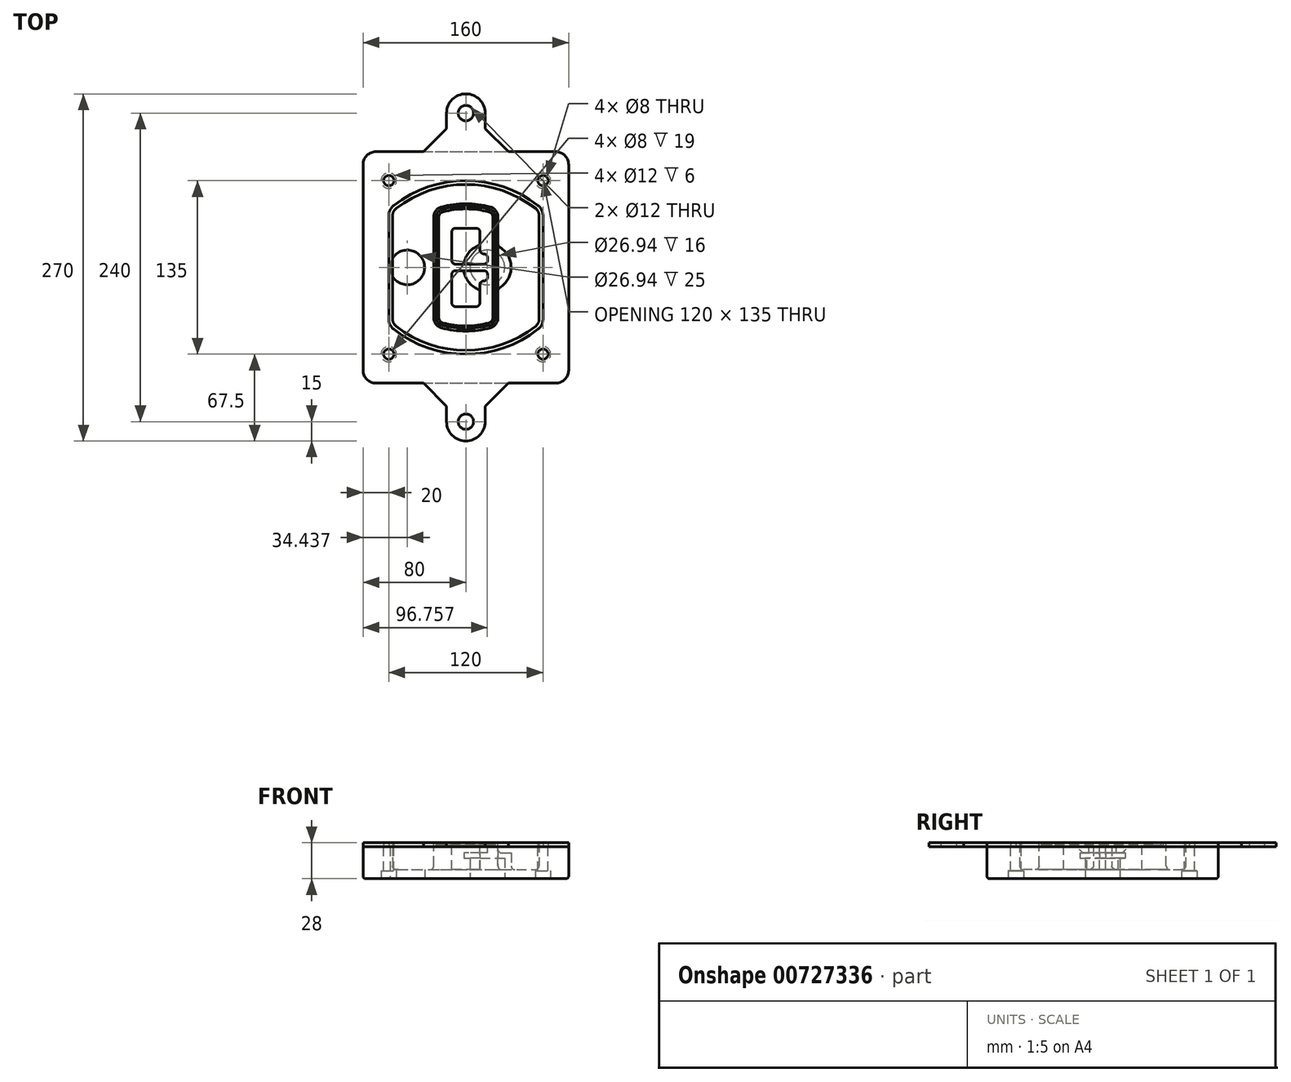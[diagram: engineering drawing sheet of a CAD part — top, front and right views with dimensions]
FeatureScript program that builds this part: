
annotation { "Feature Type Name" : "Feature", "Feature Type Description" : "" }
export const myFeature = defineFeature(function(context is Context, id is Id, definition is map)
    precondition{}
    {
        {
            var Q0;
            Q0=qCreatedBy(makeId("Top.planeOp"),FACE);
            var sketch = newSketch(context, id + "F0", { "sketchPlane" : qUnion([Q0])});
            skPoint(sketch, "E0.rect.middle", {"position": v(0, 0) * mm});
            skLineSegment(sketch, "E1.bottom", {"start": v(-70, -90) * mm, "end": v(70, -90) * mm});
            skLineSegment(sketch, "E1.top", {"start": v(-70, 90) * mm, "end": v(70, 90) * mm});
            skLineSegment(sketch, "E1.left", {"start": v(-80, -80) * mm, "end": v(-80, 80) * mm});
            skLineSegment(sketch, "E1.right", {"start": v(80, -80) * mm, "end": v(80, 80) * mm});
            skLineSegment(sketch, "E2", {"start": v(-80, 90) * mm, "end": v(80, -90) * mm, "construction": true});
            skLineSegment(sketch, "E3", {"start": v(80, 90) * mm, "end": v(-80, -90) * mm, "construction": true});
            skCircle(sketch, "E4", {"center": v(-60, 67.5) * mm, "radius": 4 * mm});
            skCircle(sketch, "E5", {"center": v(60, 67.5) * mm, "radius": 4 * mm});
            skCircle(sketch, "E6", {"center": v(60, -67.5) * mm, "radius": 4 * mm});
            skCircle(sketch, "E7", {"center": v(-60, -67.5) * mm, "radius": 4 * mm});
            skLineSegment(sketch, "E8", {"start": v(-60, 67.5) * mm, "end": v(60, 67.5) * mm, "construction": true});
            skLineSegment(sketch, "E9", {"start": v(60, 67.5) * mm, "end": v(60, -67.5) * mm, "construction": true});
            skLineSegment(sketch, "E10", {"start": v(60, -67.5) * mm, "end": v(-60, -67.5) * mm, "construction": true});
            skLineSegment(sketch, "E11", {"start": v(-60, -67.5) * mm, "end": v(-60, 67.5) * mm, "construction": true});
            skLineSegment(sketch, "E12", {"start": v(-60, 40.3) * mm, "end": v(-60, -40.3) * mm});
            skLineSegment(sketch, "E13", {"start": v(60, 40.3) * mm, "end": v(60, -40.3) * mm});
            skArc(sketch, "E14", {"start": v(56.15, 48.18) * mm, "mid": v(0, 67.5) * mm, "end": v(-56.15, 48.18) * mm});
            skArc(sketch, "E15", {"start": v(-56.15, -48.18) * mm, "mid": v(0, -67.5) * mm, "end": v(56.15, -48.18) * mm});
            skLineSegment(sketch, "E16", {"start": v(-60, 0) * mm, "end": v(60, 0) * mm, "construction": true});
            skPoint(sketch, "E17.visualSharp", {"position": v(-60, -45) * mm});
            skArc(sketch, "E17.filletArc", {"start": v(-60, -40.3) * mm, "mid": v(-58.99, -44.68) * mm, "end": v(-56.15, -48.18) * mm});
            skPoint(sketch, "E18.visualSharp", {"position": v(-60, 45) * mm});
            skArc(sketch, "E18.filletArc", {"start": v(-56.15, 48.18) * mm, "mid": v(-58.99, 44.68) * mm, "end": v(-60, 40.3) * mm});
            skPoint(sketch, "E19.visualSharp", {"position": v(60, 45) * mm});
            skArc(sketch, "E19.filletArc", {"start": v(60, 40.3) * mm, "mid": v(58.99, 44.68) * mm, "end": v(56.15, 48.18) * mm});
            skPoint(sketch, "E20.visualSharp", {"position": v(60, -45) * mm});
            skArc(sketch, "E20.filletArc", {"start": v(56.15, -48.18) * mm, "mid": v(58.99, -44.68) * mm, "end": v(60, -40.3) * mm});
            skPoint(sketch, "E21.visualSharp", {"position": v(-80, 90) * mm});
            skArc(sketch, "E21.filletArc", {"start": v(-70, 90) * mm, "mid": v(-77.07, 87.07) * mm, "end": v(-80, 80) * mm});
            skPoint(sketch, "E22.visualSharp", {"position": v(80, 90) * mm});
            skArc(sketch, "E22.filletArc", {"start": v(80, 80) * mm, "mid": v(77.07, 87.07) * mm, "end": v(70, 90) * mm});
            skPoint(sketch, "E23.visualSharp", {"position": v(80, -90) * mm});
            skArc(sketch, "E23.filletArc", {"start": v(70, -90) * mm, "mid": v(77.07, -87.07) * mm, "end": v(80, -80) * mm});
            skPoint(sketch, "E24.visualSharp", {"position": v(-80, -90) * mm});
            skArc(sketch, "E24.filletArc", {"start": v(-80, -80) * mm, "mid": v(-77.07, -87.07) * mm, "end": v(-70, -90) * mm});
            skArc(sketch, "E25.0", {"start": v(57, 40.3) * mm, "mid": v(56.3, 43.36) * mm, "end": v(54.3, 45.81) * mm});
            skLineSegment(sketch, "E25.1", {"start": v(57, 40.3) * mm, "end": v(57, -40.3) * mm});
            skArc(sketch, "E25.2", {"start": v(54.3, -45.81) * mm, "mid": v(56.3, -43.36) * mm, "end": v(57, -40.3) * mm});
            skArc(sketch, "E25.3", {"start": v(-54.3, -45.81) * mm, "mid": v(0, -64.5) * mm, "end": v(54.3, -45.81) * mm});
            skArc(sketch, "E25.4", {"start": v(-57, -40.3) * mm, "mid": v(-56.3, -43.36) * mm, "end": v(-54.3, -45.81) * mm});
            skArc(sketch, "E25.5", {"start": v(54.3, 45.81) * mm, "mid": v(0, 64.5) * mm, "end": v(-54.3, 45.81) * mm});
            skLineSegment(sketch, "E25.6", {"start": v(-57, 40.3) * mm, "end": v(-57, -40.3) * mm});
            skArc(sketch, "E25.7", {"start": v(-54.3, 45.81) * mm, "mid": v(-56.3, 43.36) * mm, "end": v(-57, 40.3) * mm});
            skArc(sketch, "E26.0", {"start": v(-58.62, 51.33) * mm, "mid": v(-62.58, 46.43) * mm, "end": v(-64, 40.3) * mm});
            skArc(sketch, "E26.1", {"start": v(58.62, 51.33) * mm, "mid": v(0, 71.5) * mm, "end": v(-58.62, 51.33) * mm});
            skArc(sketch, "E26.2", {"start": v(64, 40.3) * mm, "mid": v(62.58, 46.43) * mm, "end": v(58.62, 51.33) * mm});
            skLineSegment(sketch, "E26.3", {"start": v(64, 40.3) * mm, "end": v(64, -40.3) * mm});
            skArc(sketch, "E26.4", {"start": v(58.62, -51.33) * mm, "mid": v(62.58, -46.43) * mm, "end": v(64, -40.3) * mm});
            skLineSegment(sketch, "E26.5", {"start": v(-64, 40.3) * mm, "end": v(-64, -40.3) * mm});
            skArc(sketch, "E26.6", {"start": v(-58.62, -51.33) * mm, "mid": v(0, -71.5) * mm, "end": v(58.62, -51.33) * mm});
            skArc(sketch, "E26.7", {"start": v(-64, -40.3) * mm, "mid": v(-62.58, -46.43) * mm, "end": v(-58.62, -51.33) * mm});
            skSolve(sketch);
        }
        {
            var Q0;
            Q0=makeQuery(id+"F0.imprint","IMPRINT",FACE,{"disambiguationData":[TD([[makeQuery(id+"F0.imprint","IMPRINT",EDGE,{"derivedFrom":sQuery(id+"F0.wireOp",EDGE,"E1.bottom")}),1.0]])]});
            var Q1;
            Q1=makeQuery(id+"F0.imprint","IMPRINT",FACE,{"disambiguationData":[TD([[makeQuery(id+"F0.imprint","IMPRINT",EDGE,{"derivedFrom":sQuery(id+"F0.wireOp",EDGE,"E12")}),1.0]])]});
            var Q2;
            Q2=makeQuery(id+"F0.imprint","IMPRINT",FACE,{"disambiguationData":[TD([[makeQuery(id+"F0.imprint","IMPRINT",EDGE,{"derivedFrom":sQuery(id+"F0.wireOp",EDGE,"E25.0")}),1.0]])]});
            var Q3;
            Q3=makeQuery(id+"F0.imprint","IMPRINT",FACE,{"disambiguationData":[TD([[makeQuery(id+"F0.imprint","IMPRINT",EDGE,{"derivedFrom":sQuery(id+"F0.wireOp",EDGE,"E12")}),-1.0]])]});
            extrude(context, id + "F1", {"entities" : qUnion([Q0, Q1, Q2, Q3]), "oppositeDirection" : true, "depth" : 25 * mm});
        }
        {
            var Q0;
            Q0=makeQuery(id+"F0.imprint","IMPRINT",FACE,{"disambiguationData":[TD([[makeQuery(id+"F0.imprint","IMPRINT",EDGE,{"derivedFrom":sQuery(id+"F0.wireOp",EDGE,"E12")}),1.0]])]});
            extrude(context, id + "F2", {"entities" : qUnion([Q0]), "operationType" : NewBodyOperationType.ADD, "depth" : 3 * mm});
        }
        {
            var Q0;
            Q0=makeQuery(id+"F0.imprint","IMPRINT",FACE,{"disambiguationData":[TD([[makeQuery(id+"F0.imprint","IMPRINT",EDGE,{"derivedFrom":sQuery(id+"F0.wireOp",EDGE,"E25.0")}),1.0]])]});
            extrude(context, id + "F3", {"entities" : qUnion([Q0]), "operationType" : NewBodyOperationType.REMOVE, "oppositeDirection" : true, "depth" : 18 * mm});
        }
        {
            var Q0;
            Q0=makeQuery(id+"F2.opExtrude","CAP_FACE",FACE,{"disambiguationData":[OSD([sQuery(id+"F0.wireOp",EDGE,"E12"),sQuery(id+"F0.wireOp",EDGE,"E13"),sQuery(id+"F0.wireOp",EDGE,"E14"),sQuery(id+"F0.wireOp",EDGE,"E15"),sQuery(id+"F0.wireOp",EDGE,"E17.filletArc"),sQuery(id+"F0.wireOp",EDGE,"E18.filletArc"),sQuery(id+"F0.wireOp",EDGE,"E19.filletArc"),sQuery(id+"F0.wireOp",EDGE,"E20.filletArc"),sQuery(id+"F0.wireOp",EDGE,"E25.0"),sQuery(id+"F0.wireOp",EDGE,"E25.1"),sQuery(id+"F0.wireOp",EDGE,"E25.2"),sQuery(id+"F0.wireOp",EDGE,"E25.3"),sQuery(id+"F0.wireOp",EDGE,"E25.4"),sQuery(id+"F0.wireOp",EDGE,"E25.5"),sQuery(id+"F0.wireOp",EDGE,"E25.6"),sQuery(id+"F0.wireOp",EDGE,"E25.7")])],"isStart":false});
            var sketch = newSketch(context, id + "F4", { "sketchPlane" : qUnion([Q0])});
            skArc(sketch, "E27.0", {"start": v(-19.08, -46.97) * mm, "mid": v(0, -49.5) * mm, "end": v(19.08, -46.97) * mm});
            skArc(sketch, "E28.0", {"start": v(19.08, 46.97) * mm, "mid": v(0, 49.5) * mm, "end": v(-19.08, 46.97) * mm});
            skLineSegment(sketch, "E29", {"start": v(-25, 39.25) * mm, "end": v(-25, -39.25) * mm});
            skLineSegment(sketch, "E30", {"start": v(25, 39.25) * mm, "end": v(25, -39.25) * mm});
            skLineSegment(sketch, "E31", {"start": v(-25, 45.1) * mm, "end": v(25, 45.1) * mm, "construction": true});
            skLineSegment(sketch, "E32", {"start": v(-25, -45.1) * mm, "end": v(25, -45.1) * mm, "construction": true});
            skPoint(sketch, "E33.visualSharp", {"position": v(-25, 45.1) * mm});
            skArc(sketch, "E33.filletArc", {"start": v(-19.08, 46.97) * mm, "mid": v(-23.35, 44.11) * mm, "end": v(-25, 39.25) * mm});
            skPoint(sketch, "E34.visualSharp", {"position": v(25, 45.1) * mm});
            skArc(sketch, "E34.filletArc", {"start": v(25, 39.25) * mm, "mid": v(23.35, 44.11) * mm, "end": v(19.08, 46.97) * mm});
            skPoint(sketch, "E35.visualSharp", {"position": v(25, -45.1) * mm});
            skArc(sketch, "E35.filletArc", {"start": v(19.08, -46.97) * mm, "mid": v(23.35, -44.11) * mm, "end": v(25, -39.25) * mm});
            skPoint(sketch, "E36.visualSharp", {"position": v(-25, -45.1) * mm});
            skArc(sketch, "E36.filletArc", {"start": v(-25, -39.25) * mm, "mid": v(-23.35, -44.11) * mm, "end": v(-19.08, -46.97) * mm});
            skArc(sketch, "E37.0", {"start": v(54.3, 45.81) * mm, "mid": v(0, 64.5) * mm, "end": v(-54.3, 45.81) * mm});
            skArc(sketch, "E37.1", {"start": v(-54.3, 45.81) * mm, "mid": v(-56.3, 43.36) * mm, "end": v(-57, 40.3) * mm});
            skLineSegment(sketch, "E37.2", {"start": v(-57, 40.3) * mm, "end": v(-57, -40.3) * mm});
            skArc(sketch, "E37.3", {"start": v(-57, -40.3) * mm, "mid": v(-56.3, -43.36) * mm, "end": v(-54.3, -45.81) * mm});
            skArc(sketch, "E37.4", {"start": v(-54.3, -45.81) * mm, "mid": v(0, -64.5) * mm, "end": v(54.3, -45.81) * mm});
            skArc(sketch, "E37.5", {"start": v(54.3, -45.81) * mm, "mid": v(56.3, -43.36) * mm, "end": v(57, -40.3) * mm});
            skLineSegment(sketch, "E37.6", {"start": v(57, 40.3) * mm, "end": v(57, -40.3) * mm});
            skArc(sketch, "E37.7", {"start": v(57, 40.3) * mm, "mid": v(56.3, 43.36) * mm, "end": v(54.3, 45.81) * mm});
            skLineSegment(sketch, "E38.0", {"start": v(23, 39.25) * mm, "end": v(23, -39.25) * mm});
            skArc(sketch, "E38.1", {"start": v(18.56, -45.04) * mm, "mid": v(21.76, -42.9) * mm, "end": v(23, -39.25) * mm});
            skArc(sketch, "E38.2", {"start": v(-18.56, -45.04) * mm, "mid": v(0, -47.5) * mm, "end": v(18.56, -45.04) * mm});
            skArc(sketch, "E38.3", {"start": v(-23, -39.25) * mm, "mid": v(-21.76, -42.9) * mm, "end": v(-18.56, -45.04) * mm});
            skLineSegment(sketch, "E38.4", {"start": v(-23, 39.25) * mm, "end": v(-23, -39.25) * mm});
            skArc(sketch, "E38.5", {"start": v(23, 39.25) * mm, "mid": v(21.76, 42.9) * mm, "end": v(18.56, 45.04) * mm});
            skArc(sketch, "E38.6", {"start": v(-18.56, 45.04) * mm, "mid": v(-21.76, 42.9) * mm, "end": v(-23, 39.25) * mm});
            skArc(sketch, "E38.7", {"start": v(18.56, 45.04) * mm, "mid": v(0, 47.5) * mm, "end": v(-18.56, 45.04) * mm});
            skArc(sketch, "E39.0", {"start": v(21, 39.25) * mm, "mid": v(20.18, 41.68) * mm, "end": v(18.04, 43.1) * mm});
            skLineSegment(sketch, "E39.1", {"start": v(21, 39.25) * mm, "end": v(21, -39.25) * mm});
            skArc(sketch, "E39.2", {"start": v(18.04, -43.1) * mm, "mid": v(20.18, -41.68) * mm, "end": v(21, -39.25) * mm});
            skArc(sketch, "E39.3", {"start": v(-18.04, -43.1) * mm, "mid": v(0, -45.5) * mm, "end": v(18.04, -43.1) * mm});
            skArc(sketch, "E39.4", {"start": v(-21, -39.25) * mm, "mid": v(-20.18, -41.68) * mm, "end": v(-18.04, -43.1) * mm});
            skArc(sketch, "E39.5", {"start": v(18.04, 43.1) * mm, "mid": v(0, 45.5) * mm, "end": v(-18.04, 43.1) * mm});
            skLineSegment(sketch, "E39.6", {"start": v(-21, 39.25) * mm, "end": v(-21, -39.25) * mm});
            skArc(sketch, "E39.7", {"start": v(-18.04, 43.1) * mm, "mid": v(-20.18, 41.68) * mm, "end": v(-21, 39.25) * mm});
            skLineSegment(sketch, "E40", {"start": v(-25, 0) * mm, "end": v(25, 0) * mm, "construction": true});
            skLineSegment(sketch, "E41", {"start": v(-11, 5.5) * mm, "end": v(-11, 27.5) * mm});
            skLineSegment(sketch, "E42", {"start": v(-8, 30.5) * mm, "end": v(8, 30.5) * mm});
            skLineSegment(sketch, "E43", {"start": v(11, 27.5) * mm, "end": v(11, 13.5) * mm});
            skLineSegment(sketch, "E44", {"start": v(14, 10.5) * mm, "end": v(14, 10.5) * mm});
            skLineSegment(sketch, "E45", {"start": v(17, 7.5) * mm, "end": v(17, 5.5) * mm});
            skLineSegment(sketch, "E46", {"start": v(14, 2.5) * mm, "end": v(-8, 2.5) * mm});
            skPoint(sketch, "E47.visualSharp", {"position": v(-11, 30.5) * mm});
            skArc(sketch, "E47.filletArc", {"start": v(-8, 30.5) * mm, "mid": v(-10.12, 29.62) * mm, "end": v(-11, 27.5) * mm});
            skPoint(sketch, "E48.visualSharp", {"position": v(11, 30.5) * mm});
            skArc(sketch, "E48.filletArc", {"start": v(11, 27.5) * mm, "mid": v(10.12, 29.62) * mm, "end": v(8, 30.5) * mm});
            skPoint(sketch, "E49.visualSharp", {"position": v(11, 10.5) * mm});
            skArc(sketch, "E49.filletArc", {"start": v(11, 13.5) * mm, "mid": v(11.88, 11.38) * mm, "end": v(14, 10.5) * mm});
            skPoint(sketch, "E50.visualSharp", {"position": v(17, 10.5) * mm});
            skArc(sketch, "E50.filletArc", {"start": v(17, 7.5) * mm, "mid": v(16.12, 9.62) * mm, "end": v(14, 10.5) * mm});
            skPoint(sketch, "E51.visualSharp", {"position": v(17, 2.5) * mm});
            skArc(sketch, "E51.filletArc", {"start": v(14, 2.5) * mm, "mid": v(16.12, 3.38) * mm, "end": v(17, 5.5) * mm});
            skPoint(sketch, "E52.visualSharp", {"position": v(-11, 2.5) * mm});
            skArc(sketch, "E52.filletArc", {"start": v(-11, 5.5) * mm, "mid": v(-10.12, 3.38) * mm, "end": v(-8, 2.5) * mm});
            skLineSegment(sketch, "E53.0.MirrorCS", {"start": v(14, -2.5) * mm, "end": v(-8, -2.5) * mm});
            skArc(sketch, "E54.0.MirrorCS", {"start": v(-11, -5.5) * mm, "mid": v(-10.12, -3.38) * mm, "end": v(-8, -2.5) * mm});
            skLineSegment(sketch, "E55.0.MirrorCS", {"start": v(-11, -5.5) * mm, "end": v(-11, -27.5) * mm});
            skArc(sketch, "E56.0.MirrorCS", {"start": v(-8, -30.5) * mm, "mid": v(-10.12, -29.62) * mm, "end": v(-11, -27.5) * mm});
            skLineSegment(sketch, "E57.0.MirrorCS", {"start": v(-8, -30.5) * mm, "end": v(8, -30.5) * mm});
            skArc(sketch, "E58.0.MirrorCS", {"start": v(11, -27.5) * mm, "mid": v(10.12, -29.62) * mm, "end": v(8, -30.5) * mm});
            skLineSegment(sketch, "E59.0.MirrorCS", {"start": v(11, -27.5) * mm, "end": v(11, -13.5) * mm});
            skArc(sketch, "E60.0.MirrorCS", {"start": v(11, -13.5) * mm, "mid": v(11.88, -11.38) * mm, "end": v(14, -10.5) * mm});
            skArc(sketch, "E61.0.MirrorCS", {"start": v(17, -7.5) * mm, "mid": v(16.12, -9.62) * mm, "end": v(14, -10.5) * mm});
            skLineSegment(sketch, "E62.0.MirrorCS", {"start": v(17, -7.5) * mm, "end": v(17, -5.5) * mm});
            skArc(sketch, "E63.0.MirrorCS", {"start": v(14, -2.5) * mm, "mid": v(16.12, -3.38) * mm, "end": v(17, -5.5) * mm});
            skSolve(sketch);
        }
        {
            var Q0;
            Q0=makeQuery(id+"F4.imprint","IMPRINT",FACE,{"disambiguationData":[TD([[makeQuery(id+"F4.imprint","IMPRINT",EDGE,{"derivedFrom":sQuery(id+"F4.wireOp",EDGE,"E27.0")}),1.0]])]});
            var Q1;
            Q1=makeQuery(id+"F4.imprint","IMPRINT",FACE,{"disambiguationData":[TD([[makeQuery(id+"F4.imprint","IMPRINT",EDGE,{"derivedFrom":sQuery(id+"F4.wireOp",EDGE,"E38.0")}),-1.0]])]});
            var Q2;
            Q2=makeQuery(id+"F4.imprint","IMPRINT",FACE,{"disambiguationData":[TD([[makeQuery(id+"F4.imprint","IMPRINT",EDGE,{"derivedFrom":sQuery(id+"F4.wireOp",EDGE,"E39.0")}),1.0]])]});
            extrude(context, id + "F5", {"entities" : qUnion([Q0, Q1, Q2]), "operationType" : NewBodyOperationType.ADD, "endBound" : BoundingType.UP_TO_NEXT, "oppositeDirection" : true, "depth" : 25 * mm});
        }
        {
            var Q0;
            Q0=makeQuery(id+"F4.imprint","IMPRINT",FACE,{"disambiguationData":[TD([[makeQuery(id+"F4.imprint","IMPRINT",EDGE,{"derivedFrom":sQuery(id+"F4.wireOp",EDGE,"E38.0")}),-1.0]])]});
            extrude(context, id + "F6", {"entities" : qUnion([Q0]), "operationType" : NewBodyOperationType.REMOVE, "oppositeDirection" : true, "depth" : 2 * mm});
        }
        {
            var Q0;
            Q0=makeQuery(id+"F1.opExtrude","CAP_FACE",FACE,{"disambiguationData":[OSD([sQuery(id+"F0.wireOp",EDGE,"E1.bottom"),sQuery(id+"F0.wireOp",EDGE,"E1.top"),sQuery(id+"F0.wireOp",EDGE,"E1.left"),sQuery(id+"F0.wireOp",EDGE,"E1.right"),sQuery(id+"F0.wireOp",EDGE,"E4"),sQuery(id+"F0.wireOp",EDGE,"E5"),sQuery(id+"F0.wireOp",EDGE,"E6"),sQuery(id+"F0.wireOp",EDGE,"E7"),sQuery(id+"F0.wireOp",EDGE,"E21.filletArc"),sQuery(id+"F0.wireOp",EDGE,"E22.filletArc"),sQuery(id+"F0.wireOp",EDGE,"E23.filletArc"),sQuery(id+"F0.wireOp",EDGE,"E24.filletArc")])],"isStart":false});
            var sketch = newSketch(context, id + "F7", { "sketchPlane" : qUnion([Q0])});
            skCircle(sketch, "E64", {"center": v(16.76, 0) * mm, "radius": 13.47 * mm});
            skCircle(sketch, "E65", {"center": v(-45.56, 0) * mm, "radius": 13.47 * mm});
            skLineSegment(sketch, "E66", {"start": v(80, 0) * mm, "end": v(-80, 0) * mm});
            skCircle(sketch, "E67", {"center": v(16.76, 0) * mm, "radius": 18.47 * mm});
            skCircle(sketch, "E68", {"center": v(60, -67.5) * mm, "radius": 6 * mm});
            skCircle(sketch, "E69", {"center": v(-60, -67.5) * mm, "radius": 6 * mm});
            skCircle(sketch, "E70", {"center": v(-60, 67.5) * mm, "radius": 6 * mm});
            skCircle(sketch, "E71", {"center": v(60, 67.5) * mm, "radius": 6 * mm});
            skSolve(sketch);
        }
        {
            var Q0;
            {var subQ1=sQuery(id+"F7.wireOp",EDGE,"E66");var subQ4=sQuery(id+"F7.wireOp",EDGE,"E64");var subQ6=makeQuery(id+"F7.imprint","INTERSECT",VERTEX,{"disambiguationData":[OD(0.0)],"derivedFrom":[subQ4,subQ1]});Q0=makeQuery(id+"F7.imprint","IMPRINT",FACE,{"disambiguationData":[TD([[makeQuery(id+"F7.imprint","IMPRINT",EDGE,{"disambiguationData":[TD([[subQ6,-1.0]])],"derivedFrom":subQ4}),-1.0]])]});}
            var Q1;
            {var subQ0=sQuery(id+"F7.wireOp",EDGE,"E66");var subQ1=sQuery(id+"F7.wireOp",EDGE,"E64");var subQ3=makeQuery(id+"F7.imprint","INTERSECT",VERTEX,{"disambiguationData":[OD(0.0)],"derivedFrom":[subQ1,subQ0]});Q1=makeQuery(id+"F7.imprint","IMPRINT",FACE,{"disambiguationData":[TD([[makeQuery(id+"F7.imprint","IMPRINT",EDGE,{"disambiguationData":[TD([[subQ3,-1.0]])],"derivedFrom":subQ1}),1.0]])]});}
            var Q2;
            {var subQ0=sQuery(id+"F7.wireOp",EDGE,"E66");var subQ1=sQuery(id+"F7.wireOp",EDGE,"E64");var subQ3=makeQuery(id+"F7.imprint","INTERSECT",VERTEX,{"disambiguationData":[OD(0.0)],"derivedFrom":[subQ1,subQ0]});Q2=makeQuery(id+"F7.imprint","IMPRINT",FACE,{"disambiguationData":[TD([[makeQuery(id+"F7.imprint","IMPRINT",EDGE,{"disambiguationData":[TD([[subQ3,1.0]])],"derivedFrom":subQ1}),1.0]])]});}
            var Q3;
            {var subQ1=sQuery(id+"F7.wireOp",EDGE,"E66");var subQ4=sQuery(id+"F7.wireOp",EDGE,"E64");var subQ6=makeQuery(id+"F7.imprint","INTERSECT",VERTEX,{"disambiguationData":[OD(0.0)],"derivedFrom":[subQ4,subQ1]});Q3=makeQuery(id+"F7.imprint","IMPRINT",FACE,{"disambiguationData":[TD([[makeQuery(id+"F7.imprint","IMPRINT",EDGE,{"disambiguationData":[TD([[subQ6,1.0]])],"derivedFrom":subQ4}),-1.0]])]});}
            extrude(context, id + "F8", {"entities" : qUnion([Q0, Q1, Q2, Q3]), "operationType" : NewBodyOperationType.ADD, "oppositeDirection" : true, "depth" : 20 * mm});
        }
        {
            var Q0;
            {var subQ0=sQuery(id+"F7.wireOp",EDGE,"E66");var subQ1=sQuery(id+"F7.wireOp",EDGE,"E64");var subQ3=makeQuery(id+"F7.imprint","INTERSECT",VERTEX,{"disambiguationData":[OD(0.0)],"derivedFrom":[subQ1,subQ0]});Q0=makeQuery(id+"F7.imprint","IMPRINT",FACE,{"disambiguationData":[TD([[makeQuery(id+"F7.imprint","IMPRINT",EDGE,{"disambiguationData":[TD([[subQ3,-1.0]])],"derivedFrom":subQ1}),1.0]])]});}
            var Q1;
            {var subQ0=sQuery(id+"F7.wireOp",EDGE,"E66");var subQ1=sQuery(id+"F7.wireOp",EDGE,"E64");var subQ3=makeQuery(id+"F7.imprint","INTERSECT",VERTEX,{"disambiguationData":[OD(0.0)],"derivedFrom":[subQ1,subQ0]});Q1=makeQuery(id+"F7.imprint","IMPRINT",FACE,{"disambiguationData":[TD([[makeQuery(id+"F7.imprint","IMPRINT",EDGE,{"disambiguationData":[TD([[subQ3,1.0]])],"derivedFrom":subQ1}),1.0]])]});}
            extrude(context, id + "F9", {"entities" : qUnion([Q0, Q1]), "operationType" : NewBodyOperationType.REMOVE, "oppositeDirection" : true, "depth" : 16 * mm});
        }
        {
            var Q0;
            {var subQ0=sQuery(id+"F7.wireOp",EDGE,"E66");var subQ1=sQuery(id+"F7.wireOp",EDGE,"E65");var subQ3=makeQuery(id+"F7.imprint","INTERSECT",VERTEX,{"disambiguationData":[OD(0.0)],"derivedFrom":[subQ1,subQ0]});Q0=makeQuery(id+"F7.imprint","IMPRINT",FACE,{"disambiguationData":[TD([[makeQuery(id+"F7.imprint","IMPRINT",EDGE,{"disambiguationData":[TD([[subQ3,-1.0]])],"derivedFrom":subQ1}),1.0]])]});}
            var Q1;
            {var subQ0=sQuery(id+"F7.wireOp",EDGE,"E66");var subQ1=sQuery(id+"F7.wireOp",EDGE,"E65");var subQ3=makeQuery(id+"F7.imprint","INTERSECT",VERTEX,{"disambiguationData":[OD(0.0)],"derivedFrom":[subQ1,subQ0]});Q1=makeQuery(id+"F7.imprint","IMPRINT",FACE,{"disambiguationData":[TD([[makeQuery(id+"F7.imprint","IMPRINT",EDGE,{"disambiguationData":[TD([[subQ3,1.0]])],"derivedFrom":subQ1}),1.0]])]});}
            extrude(context, id + "F10", {"entities" : qUnion([Q0, Q1]), "operationType" : NewBodyOperationType.REMOVE, "oppositeDirection" : true, "depth" : 25 * mm});
        }
        {
            var Q0;
            Q0=makeQuery(id+"F7.imprint","IMPRINT",FACE,{"disambiguationData":[TD([[makeQuery(id+"F7.imprint","IMPRINT",EDGE,{"derivedFrom":sQuery(id+"F7.wireOp",EDGE,"E68")}),1.0]])]});
            var Q1;
            Q1=makeQuery(id+"F7.imprint","IMPRINT",FACE,{"disambiguationData":[TD([[makeQuery(id+"F7.imprint","IMPRINT",EDGE,{"derivedFrom":makeQuery(id+"F1.opExtrude","CAP_EDGE",EDGE,{"disambiguationData":[OSD([sQuery(id+"F0.wireOp",EDGE,"E5")])],"isStart":false})}),-1.0]])]});
            var Q2;
            Q2=makeQuery(id+"F7.imprint","IMPRINT",FACE,{"disambiguationData":[TD([[makeQuery(id+"F7.imprint","IMPRINT",EDGE,{"derivedFrom":sQuery(id+"F7.wireOp",EDGE,"E69")}),1.0]])]});
            var Q3;
            Q3=makeQuery(id+"F7.imprint","IMPRINT",FACE,{"disambiguationData":[TD([[makeQuery(id+"F7.imprint","IMPRINT",EDGE,{"derivedFrom":makeQuery(id+"F1.opExtrude","CAP_EDGE",EDGE,{"disambiguationData":[OSD([sQuery(id+"F0.wireOp",EDGE,"E4")])],"isStart":false})}),-1.0]])]});
            var Q4;
            Q4=makeQuery(id+"F7.imprint","IMPRINT",FACE,{"disambiguationData":[TD([[makeQuery(id+"F7.imprint","IMPRINT",EDGE,{"derivedFrom":sQuery(id+"F7.wireOp",EDGE,"E70")}),1.0]])]});
            var Q5;
            Q5=makeQuery(id+"F7.imprint","IMPRINT",FACE,{"disambiguationData":[TD([[makeQuery(id+"F7.imprint","IMPRINT",EDGE,{"derivedFrom":makeQuery(id+"F1.opExtrude","CAP_EDGE",EDGE,{"disambiguationData":[OSD([sQuery(id+"F0.wireOp",EDGE,"E7")])],"isStart":false})}),-1.0]])]});
            var Q6;
            Q6=makeQuery(id+"F7.imprint","IMPRINT",FACE,{"disambiguationData":[TD([[makeQuery(id+"F7.imprint","IMPRINT",EDGE,{"derivedFrom":sQuery(id+"F7.wireOp",EDGE,"E71")}),1.0]])]});
            var Q7;
            Q7=makeQuery(id+"F7.imprint","IMPRINT",FACE,{"disambiguationData":[TD([[makeQuery(id+"F7.imprint","IMPRINT",EDGE,{"derivedFrom":makeQuery(id+"F1.opExtrude","CAP_EDGE",EDGE,{"disambiguationData":[OSD([sQuery(id+"F0.wireOp",EDGE,"E6")])],"isStart":false})}),-1.0]])]});
            extrude(context, id + "F11", {"entities" : qUnion([Q0, Q1, Q2, Q3, Q4, Q5, Q6, Q7]), "operationType" : NewBodyOperationType.REMOVE, "oppositeDirection" : true, "depth" : 6 * mm});
        }
        {
            var Q0;
            Q0=makeQuery(id+"F9.boolean.opBoolean","COPY",FACE,{"derivedFrom":makeQuery(id+"F9.opExtrude","CAP_FACE",FACE,{"disambiguationData":[OSD([sQuery(id+"F7.wireOp",EDGE,"E64")])],"isStart":false})});
            var sketch = newSketch(context, id + "F12", { "sketchPlane" : qUnion([Q0])});
            skArc(sketch, "E72.0", {"start": v(11, 17.55) * mm, "mid": v(2.57, 11.82) * mm, "end": v(-1.54, 2.5) * mm});
            skArc(sketch, "E72.1", {"start": v(-1.54, -2.5) * mm, "mid": v(2.57, -11.82) * mm, "end": v(11, -17.55) * mm});
            skLineSegment(sketch, "E73", {"start": v(-1.54, -2.5) * mm, "end": v(14, -2.5) * mm});
            skLineSegment(sketch, "E74.0", {"start": v(14, 2.5) * mm, "end": v(-1.54, 2.5) * mm});
            skArc(sketch, "E74.1", {"start": v(14, 2.5) * mm, "mid": v(16.12, 3.38) * mm, "end": v(17, 5.5) * mm});
            skLineSegment(sketch, "E74.2", {"start": v(17, 7.5) * mm, "end": v(17, 5.5) * mm});
            skArc(sketch, "E74.3", {"start": v(17, 7.5) * mm, "mid": v(16.12, 9.62) * mm, "end": v(14, 10.5) * mm});
            skArc(sketch, "E74.4", {"start": v(11, 13.5) * mm, "mid": v(11.88, 11.38) * mm, "end": v(14, 10.5) * mm});
            skLineSegment(sketch, "E74.5", {"start": v(11, 17.55) * mm, "end": v(11, 13.5) * mm});
            skLineSegment(sketch, "E74.7", {"start": v(14, -2.5) * mm, "end": v(-1.54, -2.5) * mm});
            skArc(sketch, "E74.8", {"start": v(14, -2.5) * mm, "mid": v(16.12, -3.38) * mm, "end": v(17, -5.5) * mm});
            skLineSegment(sketch, "E74.9", {"start": v(17, -7.5) * mm, "end": v(17, -5.5) * mm});
            skArc(sketch, "E74.10", {"start": v(17, -7.5) * mm, "mid": v(16.12, -9.62) * mm, "end": v(14, -10.5) * mm});
            skArc(sketch, "E74.11", {"start": v(11, -13.5) * mm, "mid": v(11.88, -11.38) * mm, "end": v(14, -10.5) * mm});
            skLineSegment(sketch, "E74.12", {"start": v(11, -17.55) * mm, "end": v(11, -13.5) * mm});
            skPoint(sketch, "E75.orphan", {"position": v(11, -27.5) * mm});
            skPoint(sketch, "E76.orphan", {"position": v(-8, -2.5) * mm});
            skPoint(sketch, "E77.orphan", {"position": v(-8, 2.5) * mm});
            skPoint(sketch, "E78.orphan", {"position": v(11, 27.5) * mm});
            skSolve(sketch);
        }
        {
            var Q0;
            {var subQ7=sQuery(id+"F12.wireOp",EDGE,"E72.0");var subQ14=sQuery(id+"F12.wireOp",EDGE,"E72.1");var subQ16=sQuery(id+"F12.wireOp",EDGE,"E74.1");var subQ18=sQuery(id+"F12.wireOp",EDGE,"E74.8");Q0=qUnion([makeQuery(id+"F12.imprint","IMPRINT",FACE,{"disambiguationData":[TD([[makeQuery(id+"F12.imprint","IMPRINT",EDGE,{"derivedFrom":subQ7}),1.0]])]}),makeQuery(id+"F12.imprint","IMPRINT",FACE,{"disambiguationData":[TD([[makeQuery(id+"F12.imprint","IMPRINT",EDGE,{"derivedFrom":subQ14}),1.0]])]}),makeQuery(id+"F12.imprint","IMPRINT",FACE,{"disambiguationData":[TD([[makeQuery(id+"F12.imprint","IMPRINT",EDGE,{"derivedFrom":subQ16}),1.0]])]}),makeQuery(id+"F12.imprint","IMPRINT",FACE,{"disambiguationData":[TD([[makeQuery(id+"F12.imprint","IMPRINT",EDGE,{"derivedFrom":subQ18}),-1.0]])]})]);}
            var Q1;
            Q1=makeQuery(id+"F5.boolean.opBoolean","SPLIT",FACE,{"disambiguationData":[TD([makeQuery(id+"F5.opExtrude","SWEPT_FACE",FACE,{"disambiguationData":[OSD([sQuery(id+"F4.wireOp",EDGE,"E41")])]})])],"derivedFrom":makeQuery(id+"F3.boolean.opBoolean","COPY",FACE,{"derivedFrom":makeQuery(id+"F3.opExtrude","CAP_FACE",FACE,{"disambiguationData":[OSD([sQuery(id+"F0.wireOp",EDGE,"E25.0"),sQuery(id+"F0.wireOp",EDGE,"E25.1"),sQuery(id+"F0.wireOp",EDGE,"E25.2"),sQuery(id+"F0.wireOp",EDGE,"E25.3"),sQuery(id+"F0.wireOp",EDGE,"E25.4"),sQuery(id+"F0.wireOp",EDGE,"E25.5"),sQuery(id+"F0.wireOp",EDGE,"E25.6"),sQuery(id+"F0.wireOp",EDGE,"E25.7")])],"isStart":false})})});
            extrude(context, id + "F13", {"entities" : qUnion([Q0]), "operationType" : NewBodyOperationType.REMOVE, "endBound" : BoundingType.UP_TO_SURFACE, "endBoundEntityFace" : qUnion([Q1]), "depth" : 25 * mm});
        }
        {
            var Q0;
            Q0=makeQuery(id+"F3.boolean.opBoolean","COPY",EDGE,{"derivedFrom":makeQuery(id+"F3.opExtrude","CAP_EDGE",EDGE,{"disambiguationData":[OSD([sQuery(id+"F0.wireOp",EDGE,"E25.6")])],"isStart":false})});
            var Q1;
            Q1=makeQuery(id+"F8.boolean.opBoolean","INTERSECT",EDGE,{"derivedFrom":[makeQuery(id+"F5.opExtrude","SWEPT_FACE",FACE,{"disambiguationData":[OSD([sQuery(id+"F4.wireOp",EDGE,"E30")])]}),makeQuery(id+"F8.opExtrude","CAP_FACE",FACE,{"disambiguationData":[OSD([sQuery(id+"F7.wireOp",EDGE,"E67")])],"isStart":false})]});
            var Q2;
            Q2=makeQuery(id+"F8.boolean.opBoolean","INTERSECT",EDGE,{"disambiguationData":[OD(1.0)],"derivedFrom":[makeQuery(id+"F5.opExtrude","SWEPT_FACE",FACE,{"disambiguationData":[OSD([sQuery(id+"F4.wireOp",EDGE,"E30")])]}),makeQuery(id+"F8.opExtrude","SWEPT_FACE",FACE,{"disambiguationData":[OSD([sQuery(id+"F7.wireOp",EDGE,"E67")])]})]});
            var Q3;
            {var subQ0=sQuery(id+"F4.wireOp",EDGE,"E30");Q3=makeQuery(id+"F8.boolean.opBoolean","SPLIT",EDGE,{"disambiguationData":[TD([makeQuery(id+"F5.opExtrude","SWEPT_FACE",FACE,{"disambiguationData":[OSD([sQuery(id+"F4.wireOp",EDGE,"E35.filletArc")])]})])],"derivedFrom":makeQuery(id+"F5.opExtrude","CAP_EDGE",EDGE,{"disambiguationData":[OSD([subQ0])],"isStart":false})});}
            var Q4;
            {var subQ0=sQuery(id+"F0.wireOp",EDGE,"E25.7");var subQ1=sQuery(id+"F0.wireOp",EDGE,"E25.1");var subQ2=sQuery(id+"F0.wireOp",EDGE,"E25.6");var subQ3=sQuery(id+"F0.wireOp",EDGE,"E25.5");var subQ4=sQuery(id+"F0.wireOp",EDGE,"E25.4");var subQ5=sQuery(id+"F0.wireOp",EDGE,"E25.0");var subQ6=sQuery(id+"F0.wireOp",EDGE,"E25.2");var subQ7=sQuery(id+"F0.wireOp",EDGE,"E25.3");Q4=makeQuery(id+"F8.boolean.opBoolean","INTERSECT",EDGE,{"derivedFrom":[makeQuery(id+"F5.boolean.opBoolean","SPLIT",FACE,{"disambiguationData":[TD([makeQuery(id+"F2.opExtrude","SWEPT_FACE",FACE,{"disambiguationData":[OSD([subQ5])]})])],"derivedFrom":makeQuery(id+"F3.boolean.opBoolean","COPY",FACE,{"derivedFrom":makeQuery(id+"F3.opExtrude","CAP_FACE",FACE,{"disambiguationData":[OSD([subQ5,subQ1,subQ6,subQ7,subQ4,subQ3,subQ2,subQ0])],"isStart":false})})}),makeQuery(id+"F8.opExtrude","SWEPT_FACE",FACE,{"disambiguationData":[OSD([sQuery(id+"F7.wireOp",EDGE,"E67")])]})]});}
            var Q5;
            Q5=makeQuery(id+"F8.boolean.opBoolean","INTERSECT",EDGE,{"disambiguationData":[OD(0.0)],"derivedFrom":[makeQuery(id+"F5.opExtrude","SWEPT_FACE",FACE,{"disambiguationData":[OSD([sQuery(id+"F4.wireOp",EDGE,"E30")])]}),makeQuery(id+"F8.opExtrude","SWEPT_FACE",FACE,{"disambiguationData":[OSD([sQuery(id+"F7.wireOp",EDGE,"E67")])]})]});
            fillet(context, id + "F14", {"entities" : qUnion([Q0, Q1, Q2, Q3, Q4, Q5]), "radius" : 3 * mm, "tangentPropagation" : true, "allowEdgeOverflow" : false});
        }
        {
            var Q0;
            Q0=makeQuery(id+"F1.opExtrude","CAP_EDGE",EDGE,{"disambiguationData":[OSD([sQuery(id+"F0.wireOp",EDGE,"E1.bottom")])],"isStart":false});
            fillet(context, id + "F15", {"entities" : qUnion([Q0]), "radius" : 2 * mm, "tangentPropagation" : true, "allowEdgeOverflow" : false});
        }
        {
            var Q0;
            {var subQ0=sQuery(id+"F0.wireOp",EDGE,"E21.filletArc");var subQ1=sQuery(id+"F0.wireOp",EDGE,"E7");var subQ2=sQuery(id+"F0.wireOp",EDGE,"E6");var subQ3=sQuery(id+"F0.wireOp",EDGE,"E5");var subQ4=sQuery(id+"F0.wireOp",EDGE,"E4");var subQ5=sQuery(id+"F0.wireOp",EDGE,"E22.filletArc");var subQ6=sQuery(id+"F0.wireOp",EDGE,"E1.bottom");var subQ7=sQuery(id+"F0.wireOp",EDGE,"E1.right");var subQ8=sQuery(id+"F0.wireOp",EDGE,"E1.top");var subQ9=sQuery(id+"F0.wireOp",EDGE,"E1.left");var subQ10=sQuery(id+"F0.wireOp",EDGE,"E23.filletArc");var subQ11=sQuery(id+"F0.wireOp",EDGE,"E24.filletArc");Q0=makeQuery(id+"F2.boolean.opBoolean","SPLIT",FACE,{"disambiguationData":[TD([makeQuery(id+"F1.opExtrude","SWEPT_FACE",FACE,{"disambiguationData":[OSD([subQ6])]})])],"derivedFrom":makeQuery(id+"F1.opExtrude","CAP_FACE",FACE,{"disambiguationData":[OSD([subQ6,subQ8,subQ9,subQ7,subQ4,subQ3,subQ2,subQ1,subQ0,subQ5,subQ10,subQ11])],"isStart":true})});}
            var sketch = newSketch(context, id + "F16", { "sketchPlane" : qUnion([Q0])});
            skLineSegment(sketch, "E79.0", {"start": v(-80, -80) * mm, "end": v(-80, 80) * mm});
            skArc(sketch, "E79.1", {"start": v(-70, 90) * mm, "mid": v(-77.07, 87.07) * mm, "end": v(-80, 80) * mm});
            skLineSegment(sketch, "E79.2", {"start": v(-70, 90) * mm, "end": v(70, 90) * mm});
            skArc(sketch, "E79.3", {"start": v(80, 80) * mm, "mid": v(77.07, 87.07) * mm, "end": v(70, 90) * mm});
            skLineSegment(sketch, "E79.4", {"start": v(80, -80) * mm, "end": v(80, 80) * mm});
            skArc(sketch, "E79.5", {"start": v(70, -90) * mm, "mid": v(77.07, -87.07) * mm, "end": v(80, -80) * mm});
            skLineSegment(sketch, "E79.6", {"start": v(-70, -90) * mm, "end": v(70, -90) * mm});
            skArc(sketch, "E79.7", {"start": v(-80, -80) * mm, "mid": v(-77.07, -87.07) * mm, "end": v(-70, -90) * mm});
            skCircle(sketch, "E79.8", {"center": v(-60, -67.5) * mm, "radius": 4 * mm});
            skCircle(sketch, "E79.9", {"center": v(60, -67.5) * mm, "radius": 4 * mm});
            skCircle(sketch, "E79.10", {"center": v(60, 67.5) * mm, "radius": 4 * mm});
            skCircle(sketch, "E79.11", {"center": v(-60, 67.5) * mm, "radius": 4 * mm});
            skLineSegment(sketch, "E79.12", {"start": v(-60, 40.3) * mm, "end": v(-60, -40.3) * mm});
            skArc(sketch, "E79.13", {"start": v(-56.15, 48.18) * mm, "mid": v(-58.99, 44.68) * mm, "end": v(-60, 40.3) * mm});
            skArc(sketch, "E79.14", {"start": v(56.15, 48.18) * mm, "mid": v(0, 67.5) * mm, "end": v(-56.15, 48.18) * mm});
            skArc(sketch, "E79.15", {"start": v(60, 40.3) * mm, "mid": v(58.99, 44.68) * mm, "end": v(56.15, 48.18) * mm});
            skLineSegment(sketch, "E79.16", {"start": v(60, 40.3) * mm, "end": v(60, -40.3) * mm});
            skArc(sketch, "E79.17", {"start": v(56.15, -48.18) * mm, "mid": v(58.99, -44.68) * mm, "end": v(60, -40.3) * mm});
            skArc(sketch, "E79.18", {"start": v(-56.15, -48.18) * mm, "mid": v(0, -67.5) * mm, "end": v(56.15, -48.18) * mm});
            skArc(sketch, "E79.19", {"start": v(-60, -40.3) * mm, "mid": v(-58.99, -44.68) * mm, "end": v(-56.15, -48.18) * mm});
            skPoint(sketch, "E80.centerSnap0", {"position": v(0, 90) * mm});
            skLineSegment(sketch, "E81", {"start": v(-33, 90) * mm, "end": v(-15, 108) * mm});
            skLineSegment(sketch, "E82", {"start": v(-15, 108) * mm, "end": v(-15, 120) * mm});
            skLineSegment(sketch, "E83", {"start": v(33, 90) * mm, "end": v(15, 108) * mm});
            skLineSegment(sketch, "E84", {"start": v(15, 108) * mm, "end": v(15, 120) * mm});
            skArc(sketch, "E85", {"start": v(15, 120) * mm, "mid": v(0, 135) * mm, "end": v(-15, 120) * mm});
            skCircle(sketch, "E86", {"center": v(0, 120) * mm, "radius": 6 * mm});
            skLineSegment(sketch, "E87", {"start": v(0, 120) * mm, "end": v(0, 90) * mm, "construction": true});
            skLineSegment(sketch, "E88", {"start": v(-80, 0) * mm, "end": v(80, 0) * mm, "construction": true});
            skLineSegment(sketch, "E89.MirrorCS", {"start": v(15, -108) * mm, "end": v(15, -120) * mm});
            skArc(sketch, "E90.MirrorCS", {"start": v(15, -120) * mm, "mid": v(0, -135) * mm, "end": v(-15, -120) * mm});
            skLineSegment(sketch, "E91.MirrorCS", {"start": v(-15, -108) * mm, "end": v(-15, -120) * mm});
            skLineSegment(sketch, "E92.MirrorCS", {"start": v(33, -90) * mm, "end": v(15, -108) * mm});
            skLineSegment(sketch, "E93.MirrorCS", {"start": v(-33, -90) * mm, "end": v(-15, -108) * mm});
            skCircle(sketch, "E94.MirrorC", {"center": v(0, -120) * mm, "radius": 6 * mm});
            skLineSegment(sketch, "E95.MirrorCS", {"start": v(0, -120) * mm, "end": v(0, -90) * mm, "construction": true});
            skSolve(sketch);
        }
        {
            var Q0;
            {var subQ1=sQuery(id+"F16.wireOp",EDGE,"E81");Q0=makeQuery(id+"F16.imprint","IMPRINT",FACE,{"disambiguationData":[TD([[makeQuery(id+"F16.imprint","IMPRINT",EDGE,{"derivedFrom":subQ1}),-1.0]])]});}
            var Q1;
            Q1=makeQuery(id+"F16.imprint","IMPRINT",FACE,{"disambiguationData":[TD([[makeQuery(id+"F16.imprint","IMPRINT",EDGE,{"derivedFrom":sQuery(id+"F16.wireOp",EDGE,"E91.MirrorCS")}),1.0]])]});
            var Q2;
            Q2=makeQuery(id+"F16.imprint","IMPRINT",FACE,{"disambiguationData":[TD([[makeQuery(id+"F16.imprint","IMPRINT",EDGE,{"derivedFrom":sQuery(id+"F16.wireOp",EDGE,"E79.0")}),-1.0]])]});
            var Q3;
            Q3=makeQuery(id+"F2.opExtrude","CAP_FACE",FACE,{"disambiguationData":[OSD([sQuery(id+"F0.wireOp",EDGE,"E12"),sQuery(id+"F0.wireOp",EDGE,"E13"),sQuery(id+"F0.wireOp",EDGE,"E14"),sQuery(id+"F0.wireOp",EDGE,"E15"),sQuery(id+"F0.wireOp",EDGE,"E17.filletArc"),sQuery(id+"F0.wireOp",EDGE,"E18.filletArc"),sQuery(id+"F0.wireOp",EDGE,"E19.filletArc"),sQuery(id+"F0.wireOp",EDGE,"E20.filletArc"),sQuery(id+"F0.wireOp",EDGE,"E25.0"),sQuery(id+"F0.wireOp",EDGE,"E25.1"),sQuery(id+"F0.wireOp",EDGE,"E25.2"),sQuery(id+"F0.wireOp",EDGE,"E25.3"),sQuery(id+"F0.wireOp",EDGE,"E25.4"),sQuery(id+"F0.wireOp",EDGE,"E25.5"),sQuery(id+"F0.wireOp",EDGE,"E25.6"),sQuery(id+"F0.wireOp",EDGE,"E25.7")])],"isStart":false});
            extrude(context, id + "F17", {"entities" : qUnion([Q0, Q1, Q2]), "endBound" : BoundingType.UP_TO_SURFACE, "depth" : 25 * mm, "endBoundEntityFace" : qUnion([Q3]), "offsetDistance" : 25 * mm});
        }
    });
